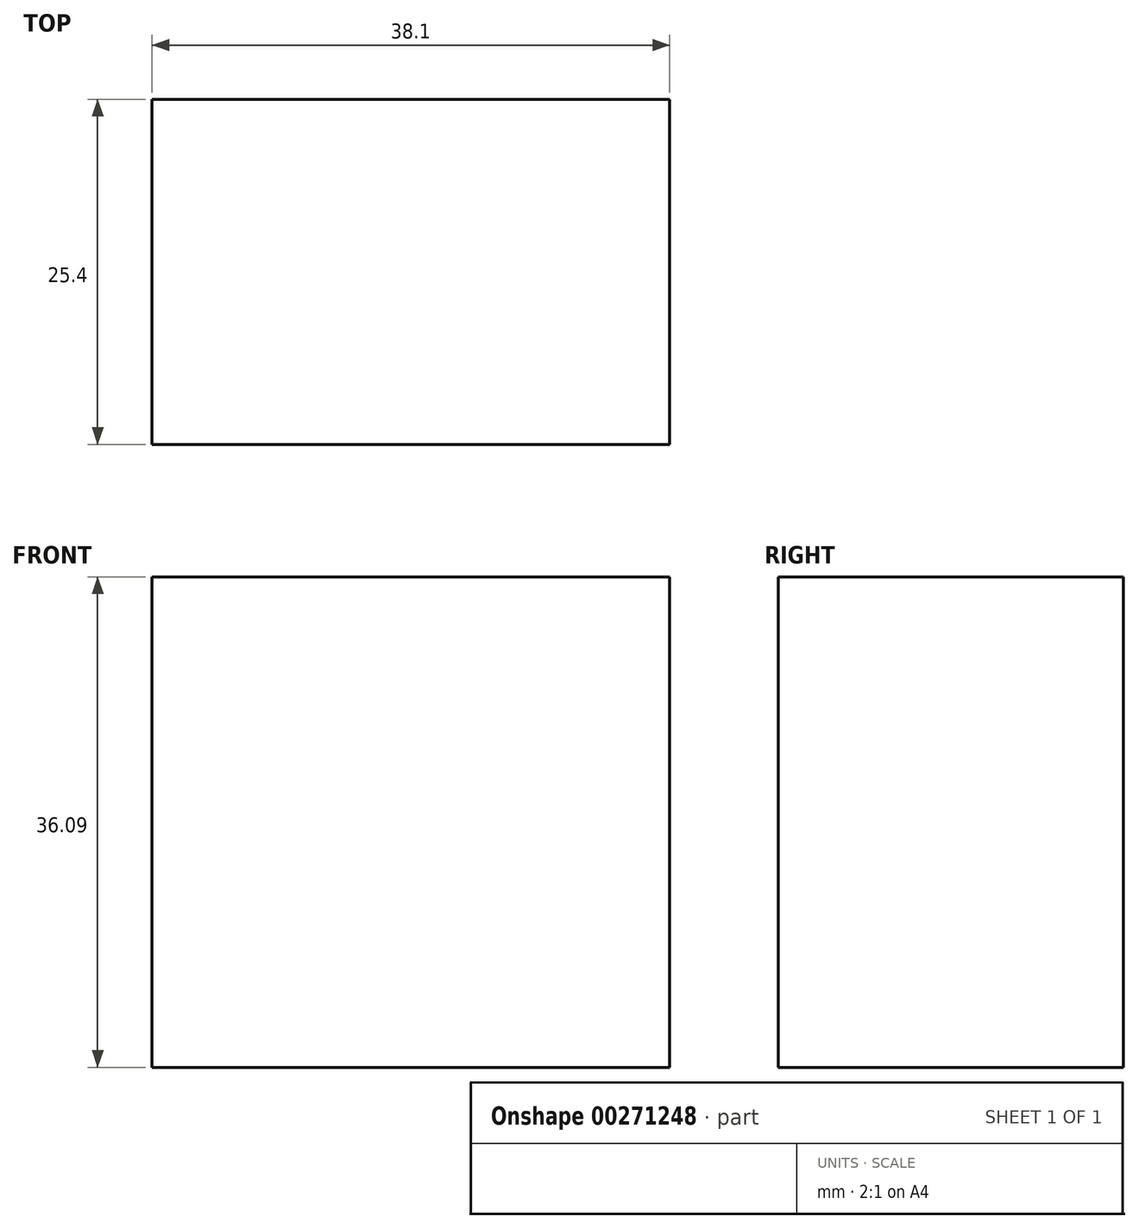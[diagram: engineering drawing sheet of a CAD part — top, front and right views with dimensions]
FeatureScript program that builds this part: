
annotation { "Feature Type Name" : "Feature", "Feature Type Description" : "" }
export const myFeature = defineFeature(function(context is Context, id is Id, definition is map)
    precondition{}
    {
        {
            var Q0;
            Q0=qCreatedBy(makeId("Front.planeOp"),FACE);
            var sketch = newSketch(context, id + "F0", { "sketchPlane" : qUnion([Q0])});
            skLineSegment(sketch, "E0", {"start": v(0, 0) * mm, "end": v(0, 36.1) * mm});
            skLineSegment(sketch, "E1", {"start": v(0, 36.1) * mm, "end": v(-38.1, 36.1) * mm});
            skLineSegment(sketch, "E2", {"start": v(-38.1, 36.1) * mm, "end": v(-38.1, 0) * mm});
            skLineSegment(sketch, "E3", {"start": v(-38.1, 0) * mm, "end": v(0, 0) * mm});
            skSolve(sketch);
        }
        {
            var Q0;
            Q0 = qSketchRegion(id + "F0", true);
            extrude(context, id + "F1", {"entities" : qUnion([Q0]), "depth" : 25.4 * mm});
        }
    });
